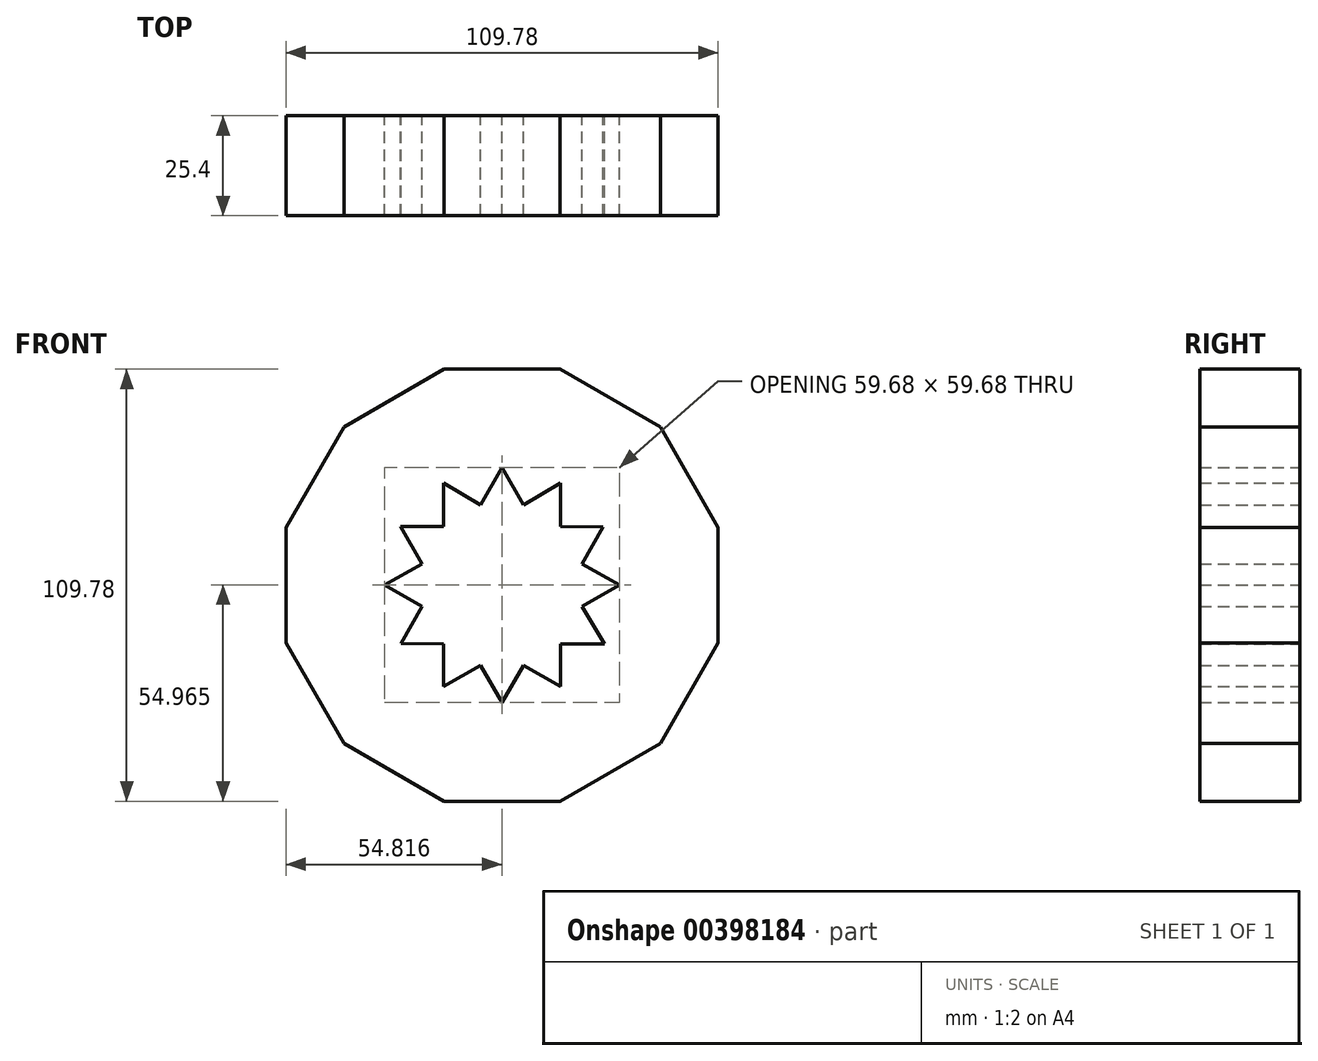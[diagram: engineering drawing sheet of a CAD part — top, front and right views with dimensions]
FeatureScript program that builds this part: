
annotation { "Feature Type Name" : "Feature", "Feature Type Description" : "" }
export const myFeature = defineFeature(function(context is Context, id is Id, definition is map)
    precondition{}
    {
        {
            var Q0;
            Q0=qCreatedBy(makeId("Front.planeOp"),FACE);
            var sketch = newSketch(context, id + "F0", { "sketchPlane" : qUnion([Q0])});
            skLineSegment(sketch, "E0.0", {"start": v(-54.89, -14.7) * mm, "end": v(-54.89, 14.7) * mm});
            skLineSegment(sketch, "E0.1", {"start": v(-54.89, 14.7) * mm, "end": v(-40.18, 40.18) * mm});
            skLineSegment(sketch, "E0.2", {"start": v(-40.18, 40.18) * mm, "end": v(-14.7, 54.89) * mm});
            skLineSegment(sketch, "E0.3", {"start": v(-14.7, 54.89) * mm, "end": v(14.7, 54.89) * mm});
            skLineSegment(sketch, "E0.4", {"start": v(14.7, 54.89) * mm, "end": v(40.18, 40.18) * mm});
            skLineSegment(sketch, "E0.5", {"start": v(40.18, 40.18) * mm, "end": v(54.89, 14.7) * mm});
            skLineSegment(sketch, "E0.6", {"start": v(54.89, 14.7) * mm, "end": v(54.89, -14.7) * mm});
            skLineSegment(sketch, "E0.7", {"start": v(54.89, -14.7) * mm, "end": v(40.18, -40.18) * mm});
            skLineSegment(sketch, "E0.8", {"start": v(40.18, -40.18) * mm, "end": v(14.7, -54.89) * mm});
            skLineSegment(sketch, "E0.9", {"start": v(14.7, -54.89) * mm, "end": v(-14.7, -54.89) * mm});
            skLineSegment(sketch, "E0.10", {"start": v(-14.7, -54.89) * mm, "end": v(-40.18, -40.18) * mm});
            skLineSegment(sketch, "E0.11", {"start": v(-40.18, -40.18) * mm, "end": v(-54.89, -14.7) * mm});
            skPoint(sketch, "E0.0.midPoint", {"position": v(-54.89, 0) * mm});
            skPoint(sketch, "E0.cCircle.center.orphan", {"position": v(0, 0) * mm});
            skLineSegment(sketch, "E1", {"start": v(-47.54, 27.44) * mm, "end": v(-25.78, 14.88) * mm});
            skLineSegment(sketch, "E2", {"start": v(0, 54.89) * mm, "end": v(0, 29.91) * mm});
            skLineSegment(sketch, "E3", {"start": v(-27.44, 47.54) * mm, "end": v(-14.96, 25.9) * mm});
            skLineSegment(sketch, "E4", {"start": v(27.44, 47.53) * mm, "end": v(14.88, 25.78) * mm});
            skLineSegment(sketch, "E5", {"start": v(-47.54, -27.44) * mm, "end": v(-25.65, -14.8) * mm});
            skLineSegment(sketch, "E6", {"start": v(-54.89, 0) * mm, "end": v(-29.91, 0) * mm});
            skArc(sketch, "E7.cCircle", {"start": v(25.9, -14.96) * mm, "mid": v(25.93, -14.92) * mm, "end": v(25.95, -14.88) * mm, "construction": true});
            skLineSegment(sketch, "E7.5", {"start": v(25.9, 14.96) * mm, "end": v(25.9, 14.96) * mm});
            skPoint(sketch, "E7.0.midPoint", {"position": v(-29.91, 0) * mm});
            skPoint(sketch, "E8.0.midPoint", {"position": v(-20.33, 0) * mm});
            skLineSegment(sketch, "E9", {"start": v(0, 29.91) * mm, "end": v(-5.45, 20.33) * mm});
            skLineSegment(sketch, "E10", {"start": v(-14.96, 25.9) * mm, "end": v(-14.88, 14.88) * mm});
            skLineSegment(sketch, "E11", {"start": v(-20.33, 5.45) * mm, "end": v(-25.78, 14.88) * mm});
            skLineSegment(sketch, "E12", {"start": v(-20.33, 5.45) * mm, "end": v(-29.91, 0) * mm});
            skLineSegment(sketch, "E13", {"start": v(-29.91, 0) * mm, "end": v(-20.33, -5.45) * mm});
            skLineSegment(sketch, "E14", {"start": v(-20.33, -5.45) * mm, "end": v(-25.65, -14.8) * mm});
            skLineSegment(sketch, "E15", {"start": v(-25.65, -14.8) * mm, "end": v(-14.88, -14.88) * mm});
            skLineSegment(sketch, "E16", {"start": v(-14.88, -14.88) * mm, "end": v(-14.88, -25.78) * mm});
            skLineSegment(sketch, "E17", {"start": v(-14.88, -25.78) * mm, "end": v(-5.45, -20.33) * mm});
            skLineSegment(sketch, "E18", {"start": v(-5.45, -20.33) * mm, "end": v(0, -29.76) * mm});
            skLineSegment(sketch, "E19", {"start": v(0, -29.76) * mm, "end": v(5.45, -20.33) * mm});
            skLineSegment(sketch, "E20", {"start": v(5.45, -20.33) * mm, "end": v(14.88, -25.78) * mm});
            skLineSegment(sketch, "E21", {"start": v(14.88, -25.78) * mm, "end": v(14.88, -14.88) * mm});
            skLineSegment(sketch, "E22", {"start": v(25.95, -14.88) * mm, "end": v(20.33, -5.45) * mm});
            skLineSegment(sketch, "E23", {"start": v(20.33, -5.45) * mm, "end": v(29.76, 0) * mm});
            skLineSegment(sketch, "E24", {"start": v(29.76, 0) * mm, "end": v(20.33, 5.45) * mm});
            skLineSegment(sketch, "E25", {"start": v(20.33, 5.45) * mm, "end": v(25.65, 14.8) * mm});
            skLineSegment(sketch, "E26", {"start": v(14.88, 14.88) * mm, "end": v(14.88, 25.9) * mm});
            skPoint(sketch, "E26.endSnap0", {"position": v(14.96, 25.9) * mm});
            skLineSegment(sketch, "E27", {"start": v(14.88, 25.9) * mm, "end": v(5.45, 20.33) * mm});
            skLineSegment(sketch, "E28", {"start": v(0, 29.91) * mm, "end": v(5.45, 20.33) * mm});
            skLineSegment(sketch, "E29", {"start": v(-25.78, 14.88) * mm, "end": v(-14.88, 14.88) * mm});
            skLineSegment(sketch, "E30", {"start": v(-14.96, 25.9) * mm, "end": v(-5.45, 20.33) * mm});
            skLineSegment(sketch, "E31.trimOffspring", {"start": v(0, -29.76) * mm, "end": v(0, -54.89) * mm});
            skLineSegment(sketch, "E32.trimOffspring", {"start": v(-14.88, -25.78) * mm, "end": v(-27.44, -47.54) * mm});
            skLineSegment(sketch, "E33.trimOffspring", {"start": v(25.78, -14.88) * mm, "end": v(47.54, -27.44) * mm});
            skLineSegment(sketch, "E34.trimOffspring", {"start": v(14.88, -25.78) * mm, "end": v(27.44, -47.54) * mm});
            skLineSegment(sketch, "E35", {"start": v(14.88, -14.88) * mm, "end": v(25.95, -14.88) * mm});
            skLineSegment(sketch, "E36.trimOffspring", {"start": v(25.65, 14.8) * mm, "end": v(47.54, 27.44) * mm});
            skPoint(sketch, "E37.orphan", {"position": v(-29.91, -8.02) * mm});
            skPoint(sketch, "E7.3.end.orphan", {"position": v(8.02, 29.91) * mm});
            skPoint(sketch, "E7.0.end.orphan", {"position": v(-29.91, 8.02) * mm});
            skPoint(sketch, "E7.1.end.orphan", {"position": v(-21.9, 21.9) * mm});
            skPoint(sketch, "E7.2.end.orphan", {"position": v(-8.02, 29.91) * mm});
            skLineSegment(sketch, "E38", {"start": v(14.88, 14.88) * mm, "end": v(25.65, 14.8) * mm});
            skPoint(sketch, "E39.orphan", {"position": v(21.9, 21.9) * mm});
            skPoint(sketch, "E40.trimOffspring.end.orphan", {"position": v(54.89, 0) * mm});
            skSolve(sketch);
        }
        {
            var Q0;
            Q0 = qSketchRegion(id + "F0", true);
            extrude(context, id + "F1", {"entities" : qUnion([Q0]), "depth" : 25.4 * mm});
        }
    });
